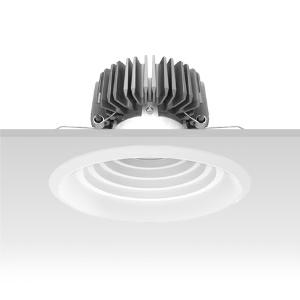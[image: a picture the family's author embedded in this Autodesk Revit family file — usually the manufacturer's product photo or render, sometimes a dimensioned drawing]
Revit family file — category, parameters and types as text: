
# Revit family: 3f_filippi_-_3f_reno_bianco_ampio_3f_filippi_-_30637_-_3f_reno_200_wh_4000-840_wide
name_source: partatom
category: Lighting Fixtures
units: mm (PartAtom-declared; Revit-internal decimal feet)

## family parameters
Cut with Voids When Loaded = No
Host = Face
Light Source = No
Part Type = Normal
Room Calculation Point = No
Round Connector Dimension = Use Diameter
Shared = No

## types (1)
- 3F Filippi - 3F Reno Bianco Ampio (1 x LED, 3521 lm, 36 W, 4000 K)
    Apparent Load = 36 VA
    Approval mark = CE
    CIE Flux Codes = 80 97 100 100 100
    Color Rendering = 80
    Color Temperature = 4000 K
    Control Gear = Electronic ballast
    Default Elevation = 1800 mm
    Description = ILLUMINOTECHNICAL
Luminous efficiency 100% (DLOR 100%, ULOR 0%).
Initial luminous flux of the luminaire 3521 lm.
Direct symmetric wide distribution.
Installation Interdistance Transv.D = 1.56 x hu - Long.D = 1.56 x hu.
Tabular UGR (CIE 117 - 4H-8H; S=0.25H; 70/50/20): RUG 21.4 - 21.4.
Beam angle: 85° - 84°.
Luminous efficacy 98 lm/W.
Lifetime (L90/B10): 30000 h. (tq+25°C)
Lifetime (L85/B10): 50000 h. (tq+25°C)
Lifetime (L70/B10): 80000 h. (tq+25°C)
Sudden decreased luminous flux after 50000 hours: 0% (C0).
Photobiological safety in compliance with IEC/TR 62778: RG1 low risk, (IEC 62471).
In compliance with IEC/EN 62722-2-1 - IEC/EN 62717 standards.

SOURCE
Compact LED module 4000/840.
Energy efficiency class (UE 2019/2020 - UE 2019/2015): E.
CIE 13.3 Colour rendering index: CRI >80 (R9 <50%).
IES TM-30 Fidelity Index: Rf = 84 Rg = 95.
CCT nominal colour temperature 4000 K.
Colour initial tolerance (MacAdam): SDCM 3.
Zhaga Book 3 compliant.

MECHANICAL
Passive heat dissipator in die-casting aluminium, oversized, for optimum thermal management of the LED module.
Parabolic element with graduated/concentric rings in white polycarbonate.
Transparent external lens with glossy and satin differentiated surfaces, with a cooling and anti-insect system in methacrylate (PMMA).
Fastening spring clips in stainless steel.
Dimensions: diameter 216 mm, height 142 mm. Weight 1.455 kg.
IP44 protection degree for exposed part, IP20 for recessed part.
Mechanical strength to impacts IK04 (0.5 joule).
Glow-wire test resistance 650°C.

ELECTRICAL
Wiring on a separate unit.
Halogen Free electronic wiring 230V-50/60Hz, power factor 0.95, THD <25%, constant output current, SELV, class II, 1 driver.
Power of the luminaire 36 W.
ENEC - CE.
SAFE FLICKER: PstLM=<1 and SVM=<0.4 (IEC TR 61547-1 and IEC TR 63158), to ensure a more comfortable and safe light.
Luminaire compliant with EN 60598-2-22 for power supply from a centralised emergency system CPSS (Central Power Supply System), not incorporated in the luminaire - high risk areas excluded. The default power and flux are 100% in AC and 100% in DC.
Ambient temperature from 0°C to +25°C.
Temperature class T6 max 85°C.
Relative humidity UR: <85%.

INSTALLATION
Pull-up recessed fitting.
False ceiling carving: 200 mm.
All accessories dedicated to this product are available on the Catalog and on our website www.3F-Filippi.com.

APPLICATIONS
Environments: architectural, commercial, exhibition areas, transit areas, corridors, shops, display windows, service areas.
In false ceilings with narrow voids.

WARNING
Luminaire designed for disposal/recycling at end-of-life.
Replaceable (LED only) light source by a professional. Replaceable control gear by a professional.
    Height = 0 mm  [stored 0 ft]
    Lamp = 1 x LED
    Lamp Light Flux = 3521 lm
    Lamp Power = 36 W
    Lamp count = 1
    Length = 216 mm
    Lifetime = 50000 h
    Luminous efficacy = 98 lm/W
    Manufacturer = 3F Filippi
    ModVariant = No
    Model = 3F Filippi - 30637 - 3F Reno 200 WH 4000-840 WIDE
    Mounting Place = Ceiling
    Mounting Type = Recessed
    Number of Poles = 1
    OnlyDefault = Yes
    Power Factor = 1
    Product Name = 3F Filippi - 3F Reno Bianco Ampio
    Product group = recessed luminaire
    ProductGroupID = 4
    Protection Class = Protection class II
    Protection Degree = IP 20
    RLX_Detail_Level = 1
    RLX_Emergency_Light_Flux = 0 lm
    RLX_Emergency_Type = 0
    RLX_Emergency_Type_DB = No
    RlxData = <blob elided: 92865 chars, md5=d769e164>
    Socket = socket
    Standby Power = 0 W
    System Light Flux = 3521 lm
    System Power = 36 W
    Type Comments = Product without accessories
    Type Image = 3ffilippi_3f_reno_200_wh_2500_3000_4000.jpg
    URL = http://relux.com
    VarID = ---
    Voltage = 0 V
    Weight = 0.00 kg
    Width = 0 mm  [stored 0 ft]

note: [stored X ft] marks values corroborated as IEEE doubles in the binary element streams (Revit-internal decimal feet)

## geometry (parser evidence)
native form markers: Blend x4, Sweep x11
no freeform markers — native parametric forms only
